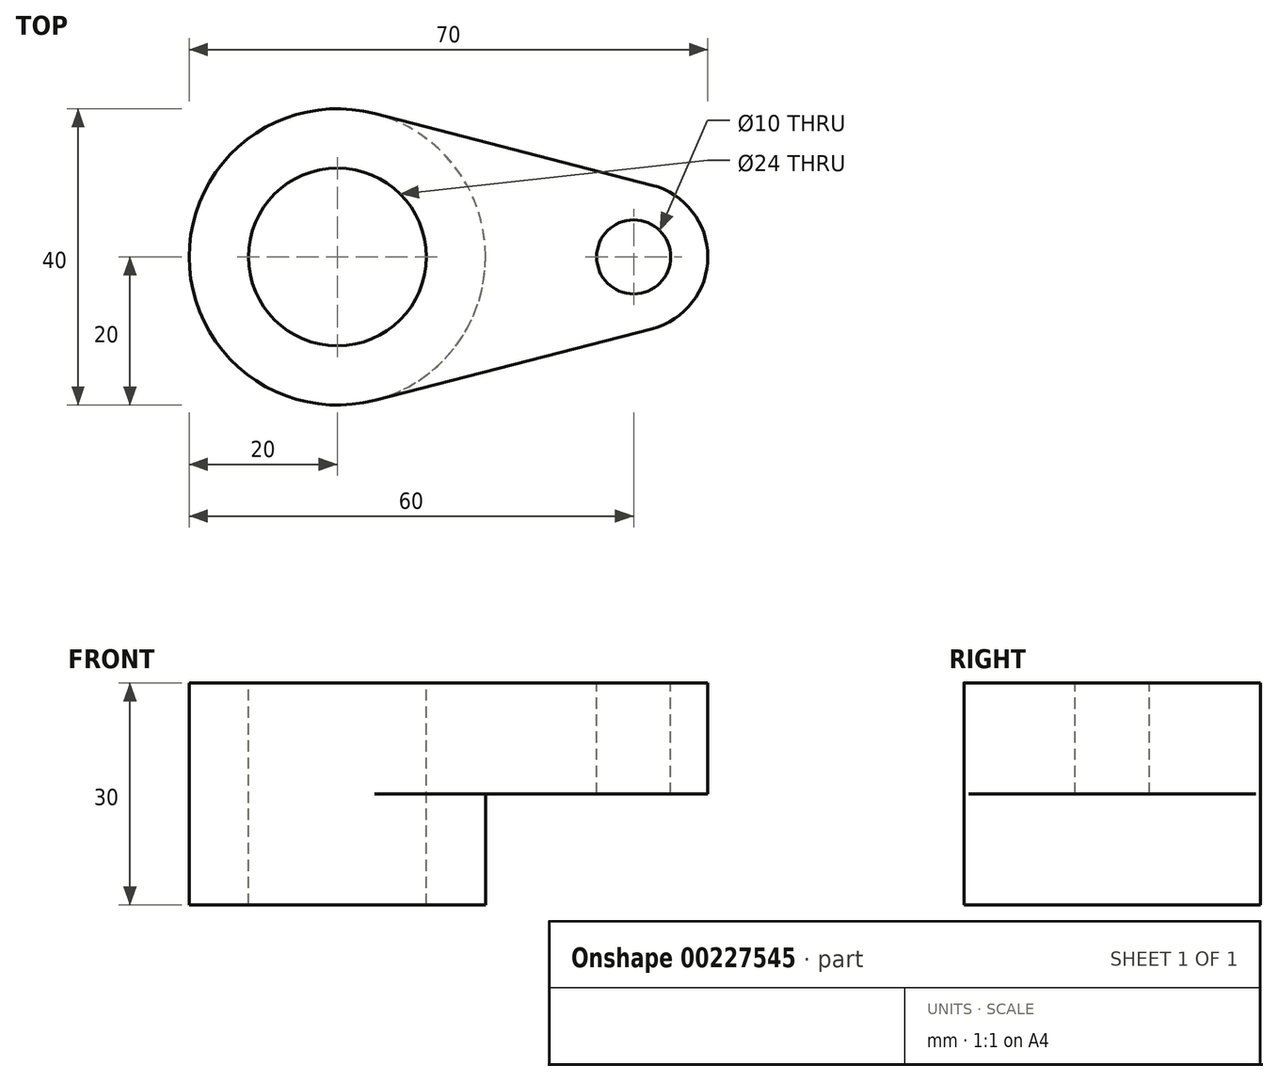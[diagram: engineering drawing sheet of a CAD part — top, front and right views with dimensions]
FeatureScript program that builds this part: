
annotation { "Feature Type Name" : "Feature", "Feature Type Description" : "" }
export const myFeature = defineFeature(function(context is Context, id is Id, definition is map)
    precondition{}
    {
        {
            var Q0;
            Q0=qCreatedBy(makeId("Top.planeOp"),FACE);
            var sketch = newSketch(context, id + "F0", { "sketchPlane" : qUnion([Q0])});
            skCircle(sketch, "E0", {"center": v(0, 0) * mm, "radius": 12 * mm});
            skCircle(sketch, "E1", {"center": v(0, 0) * mm, "radius": 20 * mm});
            skCircle(sketch, "E2", {"center": v(40, 0) * mm, "radius": 5 * mm});
            skArc(sketch, "E3", {"start": v(42.5, -9.68) * mm, "mid": v(50, 0) * mm, "end": v(42.5, 9.68) * mm});
            skLineSegment(sketch, "E4", {"start": v(5, 19.36) * mm, "end": v(42.5, 9.68) * mm});
            skLineSegment(sketch, "E5", {"start": v(5, -19.36) * mm, "end": v(42.5, -9.68) * mm});
            skSolve(sketch);
        }
        {
            var Q0;
            Q0=makeQuery(id+"F0.imprint","IMPRINT",FACE,{"disambiguationData":[TD([[makeQuery(id+"F0.imprint","IMPRINT",EDGE,{"derivedFrom":sQuery(id+"F0.wireOp",EDGE,"E2")}),-1.0]])]});
            extrude(context, id + "F1", {"entities" : qUnion([Q0]), "oppositeDirection" : true, "depth" : 15 * mm});
        }
        {
            var Q0;
            Q0=makeQuery(id+"F0.imprint","IMPRINT",FACE,{"disambiguationData":[TD([[makeQuery(id+"F0.imprint","IMPRINT",EDGE,{"derivedFrom":sQuery(id+"F0.wireOp",EDGE,"E0")}),-1.0]])]});
            extrude(context, id + "F2", {"entities" : qUnion([Q0]), "operationType" : NewBodyOperationType.ADD, "oppositeDirection" : true, "depth" : 30 * mm});
        }
    });
